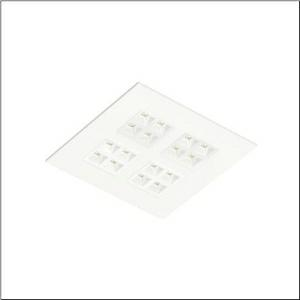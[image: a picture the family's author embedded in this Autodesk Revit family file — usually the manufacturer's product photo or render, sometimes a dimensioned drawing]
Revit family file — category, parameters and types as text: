
# Revit family: silica_r__31_square_51my6nmu44wa_c766
name_source: partatom
category: Lighting Fixtures
units: mm (PartAtom-declared; Revit-internal decimal feet)

## family parameters
Cut with Voids When Loaded = No
Host = Face
Light Source = No
Part Type = Normal
Room Calculation Point = No
Round Connector Dimension = Use Diameter
Shared = No

## types (1)
- --- (1 x LED, 6970 lm, 39 W, 4000K)
    Apparent Load = 39 VA
    CIE Flux Codes = 81 99 100 100 100
    Color Rendering = 80
    Color Temperature = 4000K
    Default Elevation = 1800 mm
    Description = Silica® 31 Square, office luminaire, primary light control with lens, of PMMA, primary anti-glare with reflector, of PC, white, light emission: direct distribution, primary light characteristic: symmetric, installation type: lay-in mounting, LED, rated luminous flux: 4.560lm, luminous efficacy: 186lm/W, light colour: 840, colour temperature: 4000K, control gear: ON/OFF Multilumen, with terminal, 3-pole, mains connection: 220..240V, AC, 50/60Hz, rated input power: 24.5W, luminaire housing, of sheet steel, coated, traffic white (RAL 9016), module: M625, length: 620mm, width: 620mm, height: 43mm, protection rating (complete): IP20, insulation class (complete): insulation class II (safety insulation), certification: CE, impact resistance: IK03, permissible operating ambient temperature: -20..+35°C, standard: EN 50419, packaging unit: 1 piece
    Height = 0 mm  [stored 0 ft]
    Lamp = 1 x LED
    Lamp Light Flux = 6970 lm
    Lamp Power = 39 W
    Lamp count = 1
    Length = 620 mm
    Luminous efficacy = 179 lm/W
    Manufacturer = Siteco
    ModVariant = No
    Model = 51MY6NMU44WA
    Mounting Place = Ceiling
    Mounting Type = Recessed
    Number of Poles = 1
    OnlyDefault = Yes
    Power Factor = 1
    Product Name = Silica® 31 Square
    Product group = office luminaire | ceiling recessed
    ProductGroupID = 401
    Protection Class = Protection class II
    Protection Degree = IP 20
    RLX_Detail_Level = 1
    RLX_Emergency_Light_Flux = 0 lm
    RLX_Emergency_Type = 0
    RLX_Emergency_Type_DB = No
    RlxData = <blob elided: 28565 chars, md5=00657d0b>
    Socket = socket
    Standby Power = 0 W
    System Light Flux = 6970 lm
    System Power = 39 W
    Type Comments = factory setting: luminous flux: 100 % | (ON | ON | ON | ON) | 1100 mA
    Type Image = l_1313651.jpg
    URL = http://relux.com
    VarID = @adj_036112
    Voltage = 0 V
    Weight = 0.00 kg
    Width = 620 mm

note: [stored X ft] marks values corroborated as IEEE doubles in the binary element streams (Revit-internal decimal feet)

## geometry (parser evidence)
native form markers: Blend x4, Sweep x9
no freeform markers — native parametric forms only
